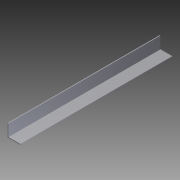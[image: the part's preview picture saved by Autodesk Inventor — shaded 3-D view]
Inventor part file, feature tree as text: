
AUTODESK INVENTOR PART (.ipt)
format: ipt  version: 2012 (Build 160160000, 160)  size: 74,240 bytes
history: native  units: in
note: dims shown in document units (in); Inventor stores cm internally (conversion verified against a paired STEP export)
features: extrude x1, sketch x1
ambient origin geometry x8: Origin, YZ Plane, XZ Plane, XY Plane, X Axis, Y Axis, Z Axis, Center Point
bodies: Solid1 (feature_tree)
feature tree (2):
  extrude  "Extrusion1"  Depth=1.0in
  sketch  "Sketch1"  dims[d0=1.0in d1=1.0in d2=0.0625in d3=0.0625in d4=12.0in d5=0.0in]
